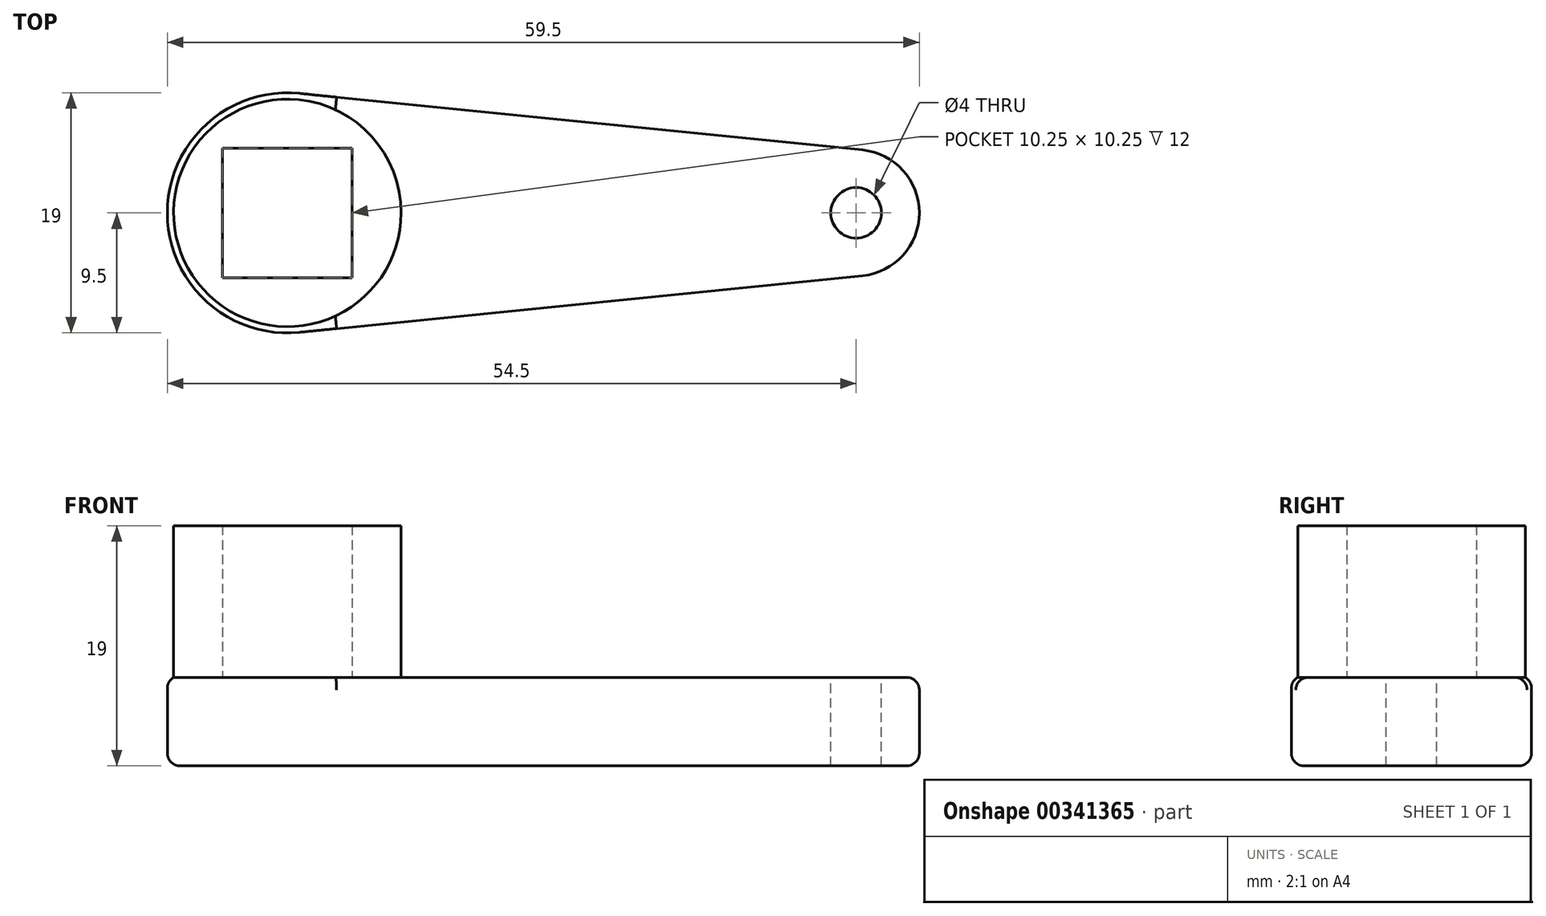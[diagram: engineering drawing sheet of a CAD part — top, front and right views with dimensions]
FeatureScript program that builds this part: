
annotation { "Feature Type Name" : "Feature", "Feature Type Description" : "" }
export const myFeature = defineFeature(function(context is Context, id is Id, definition is map)
    precondition{}
    {
        {
            var Q0;
            Q0=qCreatedBy(makeId("Top.planeOp"),FACE);
            var sketch = newSketch(context, id + "F0", { "sketchPlane" : qUnion([Q0])});
            skArc(sketch, "E0", {"start": v(0.95, 9.45) * mm, "mid": v(-9.5, 0) * mm, "end": v(0.95, -9.45) * mm});
            skLineSegment(sketch, "E1", {"start": v(0.95, 9.45) * mm, "end": v(45.5, 4.97) * mm});
            skLineSegment(sketch, "E2", {"start": v(0.95, -9.45) * mm, "end": v(45.5, -4.97) * mm});
            skArc(sketch, "E3", {"start": v(45.5, -4.97) * mm, "mid": v(50, 0) * mm, "end": v(45.5, 4.97) * mm});
            skSolve(sketch);
        }
        {
            var Q0;
            Q0=qSketchRegion(id+"F0",true);
            var Q1;
            Q1=makeQuery(id+"F0.imprint","IMPRINT",FACE,{"disambiguationData":[TD([[makeQuery(id+"F0.imprint","IMPRINT",EDGE,{"derivedFrom":sQuery(id+"F0.wireOp",EDGE,"E0")}),1.0]])]});
            extrude(context, id + "F1", {"entities" : qUnion([Q0, Q1]), "depth" : 7 * mm});
        }
        {
            var Q0;
            Q0=makeQuery(id+"F1.opExtrude","CAP_FACE",FACE,{"disambiguationData":[OSD([sQuery(id+"F0.wireOp",EDGE,"E0"),sQuery(id+"F0.wireOp",EDGE,"E1"),sQuery(id+"F0.wireOp",EDGE,"E2"),sQuery(id+"F0.wireOp",EDGE,"E3")])],"isStart":false});
            var sketch = newSketch(context, id + "F2", { "sketchPlane" : qUnion([Q0])});
            skCircle(sketch, "E4", {"center": v(0, 0) * mm, "radius": 9 * mm});
            skCircle(sketch, "E5", {"center": v(45, 0) * mm, "radius": 2 * mm});
            skCircle(sketch, "E6.cCircle", {"center": v(0, 0) * mm, "radius": 5.12 * mm, "construction": true});
            skLineSegment(sketch, "E6.0", {"start": v(5.13, -5.12) * mm, "end": v(-5.12, -5.13) * mm});
            skLineSegment(sketch, "E6.1", {"start": v(-5.12, -5.13) * mm, "end": v(-5.13, 5.12) * mm});
            skLineSegment(sketch, "E6.2", {"start": v(-5.13, 5.12) * mm, "end": v(5.12, 5.13) * mm});
            skLineSegment(sketch, "E6.3", {"start": v(5.12, 5.13) * mm, "end": v(5.13, -5.12) * mm});
            skPoint(sketch, "E6.0.midPoint", {"position": v(0, -5.12) * mm});
            skSolve(sketch);
        }
        {
            var Q0;
            Q0=makeQuery(id+"F2.imprint","IMPRINT",FACE,{"disambiguationData":[TD([[makeQuery(id+"F2.imprint","IMPRINT",EDGE,{"derivedFrom":sQuery(id+"F2.wireOp",EDGE,"E5")}),1.0]])]});
            extrude(context, id + "F3", {"entities" : qUnion([Q0]), "operationType" : NewBodyOperationType.REMOVE, "oppositeDirection" : true, "depth" : 25 * mm});
        }
        {
            var Q0;
            Q0=makeQuery(id+"F2.imprint","IMPRINT",FACE,{"disambiguationData":[TD([[makeQuery(id+"F2.imprint","IMPRINT",EDGE,{"derivedFrom":sQuery(id+"F2.wireOp",EDGE,"E4")}),1.0]])]});
            extrude(context, id + "F4", {"entities" : qUnion([Q0]), "operationType" : NewBodyOperationType.ADD, "depth" : 12 * mm});
        }
        {
            var Q0;
            Q0=makeQuery(id+"F1.opExtrude","CAP_EDGE",EDGE,{"disambiguationData":[OSD([sQuery(id+"F0.wireOp",EDGE,"E2")])],"isStart":true});
            var Q1;
            Q1=makeQuery(id+"F1.opExtrude","CAP_EDGE",EDGE,{"disambiguationData":[OSD([sQuery(id+"F0.wireOp",EDGE,"E2")])],"isStart":false});
            fillet(context, id + "F5", {"entities" : qUnion([Q0, Q1]), "radius" : 1 * mm, "tangentPropagation" : true, "allowEdgeOverflow" : false});
        }
    });
